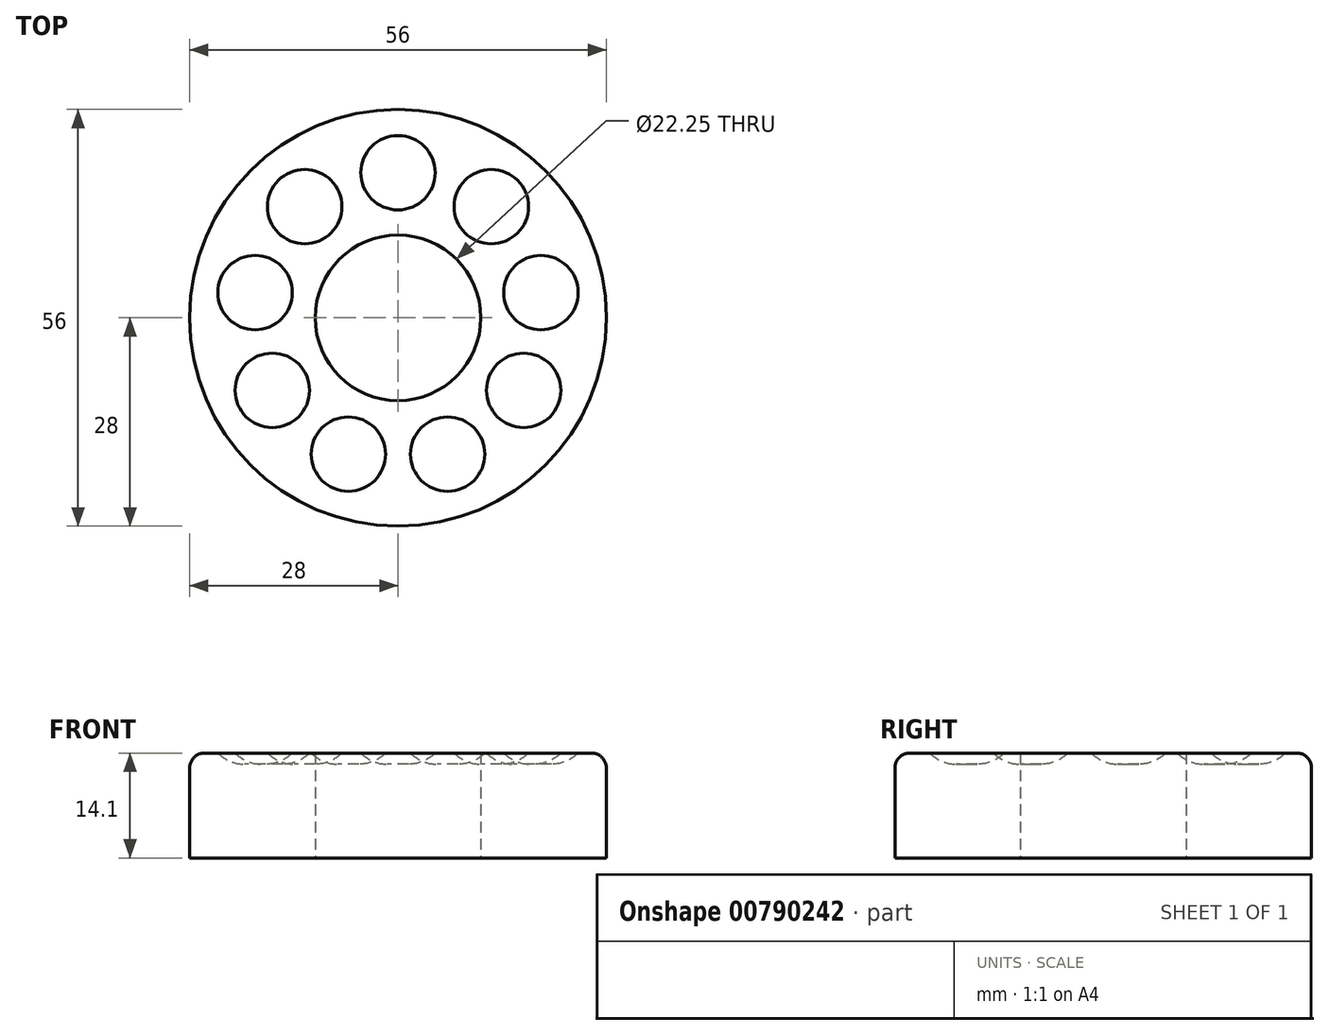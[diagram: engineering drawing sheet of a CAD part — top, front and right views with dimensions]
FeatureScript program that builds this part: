
annotation { "Feature Type Name" : "Feature", "Feature Type Description" : "" }
export const myFeature = defineFeature(function(context is Context, id is Id, definition is map)
    precondition{}
    {
        {
            var Q0;
            Q0=qCreatedBy(makeId("Top.planeOp"),FACE);
            var sketch = newSketch(context, id + "F0", { "sketchPlane" : qUnion([Q0])});
            skCircle(sketch, "E0", {"center": v(0, 0) * mm, "radius": 28 * mm});
            skCircle(sketch, "E1", {"center": v(0, 0) * mm, "radius": 11.12 * mm});
            skSolve(sketch);
        }
        {
            var Q0;
            Q0=qSketchRegion(id+"F0",true);
            extrude(context, id + "F1", {"entities" : qUnion([Q0]), "depth" : 14.1 * mm, "offsetDistance" : 25 * mm});
        }
        {
            var Q0;
            Q0=makeQuery(id+"F1.opExtrude","CAP_EDGE",EDGE,{"disambiguationData":[OSD([sQuery(id+"F0.wireOp",EDGE,"E0")])],"isStart":false});
            fillet(context, id + "F2", {"entities" : qUnion([Q0]), "radius" : 2 * mm, "tangentPropagation" : true, "allowEdgeOverflow" : false});
        }
        {
            var Q0;
            Q0=makeQuery(id+"F1.opExtrude","CAP_FACE",FACE,{"disambiguationData":[OSD([sQuery(id+"F0.wireOp",EDGE,"E0"),sQuery(id+"F0.wireOp",EDGE,"E1")])],"isStart":false});
            var sketch = newSketch(context, id + "F3", { "sketchPlane" : qUnion([Q0])});
            skCircle(sketch, "E2", {"center": v(0, 19.5) * mm, "radius": 5 * mm});
            skCircle(sketch, "E3.1.0", {"center": v(-12.53, 14.94) * mm, "radius": 5 * mm});
            skCircle(sketch, "E3.2.0", {"center": v(-19.2, 3.39) * mm, "radius": 5 * mm});
            skCircle(sketch, "E3.3.0", {"center": v(-16.89, -9.75) * mm, "radius": 5 * mm});
            skCircle(sketch, "E3.4.0", {"center": v(-6.67, -18.32) * mm, "radius": 5 * mm});
            skCircle(sketch, "E3.5.0", {"center": v(6.67, -18.32) * mm, "radius": 5 * mm});
            skCircle(sketch, "E3.6.0", {"center": v(16.89, -9.75) * mm, "radius": 5 * mm});
            skCircle(sketch, "E3.7.0", {"center": v(19.2, 3.39) * mm, "radius": 5 * mm});
            skCircle(sketch, "E3.8.0", {"center": v(12.53, 14.94) * mm, "radius": 5 * mm});
            skPoint(sketch, "E3.center", {"position": v(0, 0) * mm});
            skSolve(sketch);
        }
        {
            var Q0;
            Q0=qSketchRegion(id+"F3",true);
            extrude(context, id + "F4", {"entities" : qUnion([Q0]), "operationType" : NewBodyOperationType.REMOVE, "oppositeDirection" : true, "depth" : 1.5 * mm, "offsetDistance" : 25 * mm});
        }
        {
            var Q0;
            Q0=makeQuery(id+"F4.boolean.opBoolean","COPY",FACE,{"derivedFrom":makeQuery(id+"F4.opExtrude","CAP_FACE",FACE,{"disambiguationData":[OSD([sQuery(id+"F3.wireOp",EDGE,"E2")])],"isStart":false})});
            var Q1;
            Q1=makeQuery(id+"F4.boolean.opBoolean","COPY",FACE,{"derivedFrom":makeQuery(id+"F4.opExtrude","CAP_FACE",FACE,{"disambiguationData":[OSD([sQuery(id+"F3.wireOp",EDGE,"E3.1.0")])],"isStart":false})});
            var Q2;
            Q2=makeQuery(id+"F4.boolean.opBoolean","COPY",FACE,{"derivedFrom":makeQuery(id+"F4.opExtrude","CAP_FACE",FACE,{"disambiguationData":[OSD([sQuery(id+"F3.wireOp",EDGE,"E3.2.0")])],"isStart":false})});
            var Q3;
            Q3=makeQuery(id+"F4.boolean.opBoolean","COPY",FACE,{"derivedFrom":makeQuery(id+"F4.opExtrude","CAP_FACE",FACE,{"disambiguationData":[OSD([sQuery(id+"F3.wireOp",EDGE,"E3.3.0")])],"isStart":false})});
            var Q4;
            Q4=makeQuery(id+"F4.boolean.opBoolean","COPY",FACE,{"derivedFrom":makeQuery(id+"F4.opExtrude","CAP_FACE",FACE,{"disambiguationData":[OSD([sQuery(id+"F3.wireOp",EDGE,"E3.4.0")])],"isStart":false})});
            var Q5;
            Q5=makeQuery(id+"F4.boolean.opBoolean","COPY",FACE,{"derivedFrom":makeQuery(id+"F4.opExtrude","CAP_FACE",FACE,{"disambiguationData":[OSD([sQuery(id+"F3.wireOp",EDGE,"E3.5.0")])],"isStart":false})});
            var Q6;
            Q6=makeQuery(id+"F4.boolean.opBoolean","COPY",FACE,{"derivedFrom":makeQuery(id+"F4.opExtrude","CAP_FACE",FACE,{"disambiguationData":[OSD([sQuery(id+"F3.wireOp",EDGE,"E3.6.0")])],"isStart":false})});
            var Q7;
            Q7=makeQuery(id+"F4.boolean.opBoolean","COPY",FACE,{"derivedFrom":makeQuery(id+"F4.opExtrude","CAP_FACE",FACE,{"disambiguationData":[OSD([sQuery(id+"F3.wireOp",EDGE,"E3.7.0")])],"isStart":false})});
            var Q8;
            Q8=makeQuery(id+"F4.boolean.opBoolean","COPY",FACE,{"derivedFrom":makeQuery(id+"F4.opExtrude","CAP_FACE",FACE,{"disambiguationData":[OSD([sQuery(id+"F3.wireOp",EDGE,"E3.8.0")])],"isStart":false})});
            fillet(context, id + "F5", {"entities" : qUnion([Q0, Q1, Q2, Q3, Q4, Q5, Q6, Q7, Q8]), "radius" : 5 * mm, "tangentPropagation" : true, "allowEdgeOverflow" : false});
        }
    });
